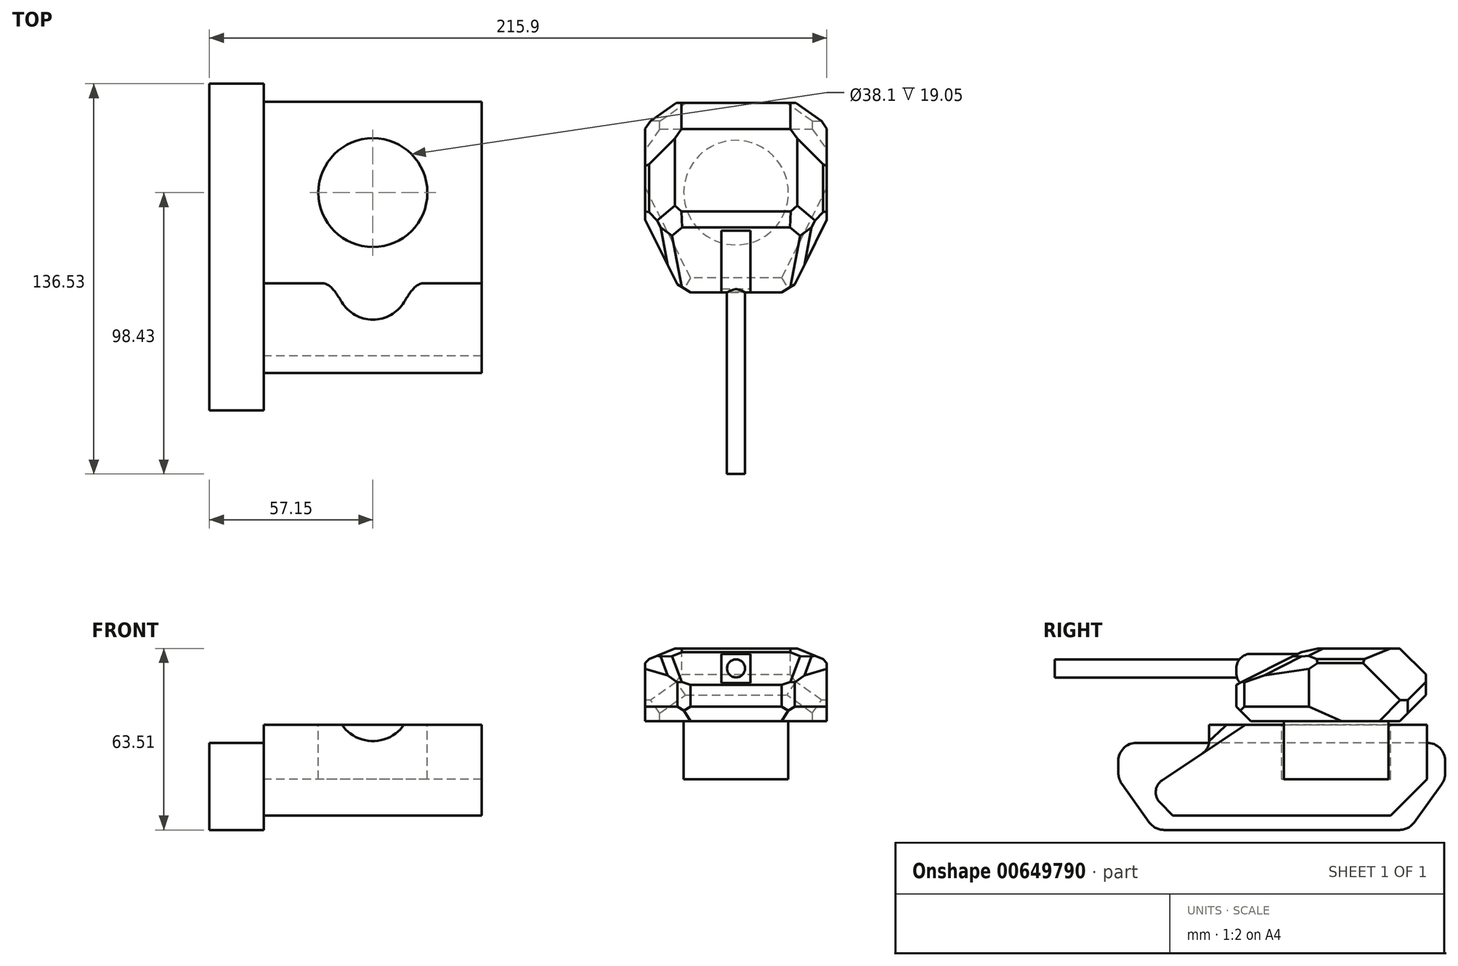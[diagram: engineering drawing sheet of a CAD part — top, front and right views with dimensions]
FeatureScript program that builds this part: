
annotation { "Feature Type Name" : "Feature", "Feature Type Description" : "" }
export const myFeature = defineFeature(function(context is Context, id is Id, definition is map)
    precondition{}
    {
        {
            var Q0;
            Q0=qCreatedBy(makeId("Right.planeOp"),FACE);
            var sketch = newSketch(context, id + "F0", { "sketchPlane" : qUnion([Q0])});
            skLineSegment(sketch, "E0.bottom", {"start": v(-50.8, -15.87) * mm, "end": v(50.8, -15.87) * mm});
            skLineSegment(sketch, "E0.top", {"start": v(-50.8, 15.88) * mm, "end": v(50.8, 15.88) * mm});
            skLineSegment(sketch, "E0.left", {"start": v(-50.8, -15.87) * mm, "end": v(-50.8, 15.88) * mm});
            skLineSegment(sketch, "E0.right", {"start": v(50.8, -15.87) * mm, "end": v(50.8, 15.88) * mm});
            skPoint(sketch, "E0.middle", {"position": v(0, 0) * mm});
            skSolve(sketch);
        }
        {
            var Q0;
            Q0=makeQuery(id+"F0.imprint","IMPRINT",FACE,{"disambiguationData":[TD([[makeQuery(id+"F0.imprint","IMPRINT",EDGE,{"derivedFrom":sQuery(id+"F0.wireOp",EDGE,"E0.bottom")}),1.0]])]});
            extrude(context, id + "F1", {"entities" : qUnion([Q0]), "endBound" : BoundingType.SYMMETRIC, "depth" : 76.2 * mm, "offsetDistance" : 25.4 * mm});
        }
        {
            var Q0;
            Q0=makeQuery(id+"F1.opExtrude","CAP_FACE",FACE,{"disambiguationData":[OSD([sQuery(id+"F0.wireOp",EDGE,"E0.bottom"),sQuery(id+"F0.wireOp",EDGE,"E0.top"),sQuery(id+"F0.wireOp",EDGE,"E0.left"),sQuery(id+"F0.wireOp",EDGE,"E0.right")])],"isStart":true});
            var sketch = newSketch(context, id + "F2", { "sketchPlane" : qUnion([Q0])});
            skLineSegment(sketch, "E1", {"start": v(-57.15, 9.52) * mm, "end": v(-57.15, -3.18) * mm});
            skLineSegment(sketch, "E2", {"start": v(-57.15, 9.52) * mm, "end": v(57.15, 9.52) * mm});
            skLineSegment(sketch, "E3", {"start": v(57.15, 9.52) * mm, "end": v(57.15, -3.18) * mm});
            skLineSegment(sketch, "E4", {"start": v(57.15, -3.18) * mm, "end": v(44.45, -20.95) * mm});
            skLineSegment(sketch, "E5", {"start": v(44.45, -20.95) * mm, "end": v(-44.45, -20.95) * mm});
            skLineSegment(sketch, "E6", {"start": v(-57.15, -3.18) * mm, "end": v(-44.45, -20.96) * mm});
            skSolve(sketch);
        }
        {
            var Q0;
            Q0=makeQuery(id+"F1.opExtrude","SWEPT_EDGE",EDGE,{"disambiguationData":[OSD([sQuery(id+"F0.wireOp",EDGE,"E0.bottom"),sQuery(id+"F0.wireOp",EDGE,"E0.left")])]});
            var Q1;
            Q1=makeQuery(id+"F1.opExtrude","SWEPT_EDGE",EDGE,{"disambiguationData":[OSD([sQuery(id+"F0.wireOp",EDGE,"E0.bottom"),sQuery(id+"F0.wireOp",EDGE,"E0.right")])]});
            chamfer(context, id + "F3", {"entities" : qUnion([Q0, Q1]), "width" : 12.7 * mm, "tangentPropagation" : true});
        }
        {
            var Q0;
            Q0 = qSketchRegion(id + "F2", true);
            extrude(context, id + "F4", {"entities" : qUnion([Q0]), "operationType" : NewBodyOperationType.ADD, "depth" : 19.05 * mm, "offsetDistance" : 25.4 * mm});
        }
        {
            var Q0;
            Q0=makeQuery(id+"F4.opExtrude","SWEPT_EDGE",EDGE,{"disambiguationData":[OSD([sQuery(id+"F2.wireOp",EDGE,"E4"),sQuery(id+"F2.wireOp",EDGE,"E5")])]});
            var Q1;
            Q1=makeQuery(id+"F4.opExtrude","SWEPT_EDGE",EDGE,{"disambiguationData":[OSD([sQuery(id+"F2.wireOp",EDGE,"E3"),sQuery(id+"F2.wireOp",EDGE,"E4")])]});
            var Q2;
            Q2=makeQuery(id+"F4.opExtrude","SWEPT_EDGE",EDGE,{"disambiguationData":[OSD([sQuery(id+"F2.wireOp",EDGE,"E2"),sQuery(id+"F2.wireOp",EDGE,"E3")])]});
            var Q3;
            Q3=makeQuery(id+"F4.opExtrude","SWEPT_EDGE",EDGE,{"disambiguationData":[OSD([sQuery(id+"F2.wireOp",EDGE,"E1"),sQuery(id+"F2.wireOp",EDGE,"E2")])]});
            var Q4;
            Q4=makeQuery(id+"F4.opExtrude","SWEPT_EDGE",EDGE,{"disambiguationData":[OSD([sQuery(id+"F2.wireOp",EDGE,"E1"),sQuery(id+"F2.wireOp",EDGE,"E6")])]});
            var Q5;
            Q5=makeQuery(id+"F4.opExtrude","SWEPT_EDGE",EDGE,{"disambiguationData":[OSD([sQuery(id+"F2.wireOp",EDGE,"E5"),sQuery(id+"F2.wireOp",EDGE,"E6")])]});
            fillet(context, id + "F5", {"entities" : qUnion([Q0, Q1, Q2, Q3, Q4, Q5]), "radius" : 6.35 * mm, "tangentPropagation" : true, "allowEdgeOverflow" : false});
        }
        {
            var Q0;
            Q0=makeQuery(id+"F1.opExtrude","SWEPT_EDGE",EDGE,{"disambiguationData":[OSD([sQuery(id+"F0.wireOp",EDGE,"E0.top"),sQuery(id+"F0.wireOp",EDGE,"E0.left")])]});
            chamfer(context, id + "F6", {"entities" : qUnion([Q0]), "chamferType" : ChamferType.TWO_OFFSETS, "width1" : 25.4 * mm, "oppositeDirection" : false, "width2" : 38.1 * mm, "tangentPropagation" : true});
        }
        {
            var Q0;
            {var subQ0=sQuery(id+"F0.wireOp",EDGE,"E0.left");Q0=makeQuery(id+"F6.opChamfer","BLEND_EDGE",EDGE,{"blendedFrom":[makeQuery(id+"F1.opExtrude","SWEPT_EDGE",EDGE,{"disambiguationData":[OSD([sQuery(id+"F0.wireOp",EDGE,"E0.top"),subQ0])]}),makeQuery(id+"F3.opChamfer","BLEND_FACE",FACE,{"disambiguationData":[OSD([sQuery(id+"F0.wireOp",EDGE,"E0.bottom"),subQ0])]})],"blendedInto":[makeQuery(id+"F3.opChamfer","BLEND_FACE",FACE,{"disambiguationData":[OSD([sQuery(id+"F0.wireOp",EDGE,"E0.bottom"),subQ0])]})]});}
            fillet(context, id + "F7", {"entities" : qUnion([Q0]), "radius" : 5.08 * mm, "tangentPropagation" : true, "allowEdgeOverflow" : false});
        }
        {
            var Q0;
            Q0=makeQuery(id+"F1.opExtrude","SWEPT_FACE",FACE,{"disambiguationData":[OSD([sQuery(id+"F0.wireOp",EDGE,"E0.top")])]});
            var sketch = newSketch(context, id + "F8", { "sketchPlane" : qUnion([Q0])});
            skCircle(sketch, "E7", {"center": v(0, 19.05) * mm, "radius": 19.05 * mm});
            skPoint(sketch, "E7.centerSnap0", {"position": v(0, -12.7) * mm});
            skPoint(sketch, "E7.centerSnap1", {"position": v(-38.1, 19.05) * mm});
            skSolve(sketch);
        }
        {
            var Q0;
            Q0=makeQuery(id+"F8.imprint","IMPRINT",FACE,{"disambiguationData":[TD([[makeQuery(id+"F8.imprint","IMPRINT",EDGE,{"derivedFrom":sQuery(id+"F8.wireOp",EDGE,"E7")}),1.0]])]});
            extrude(context, id + "F9", {"entities" : qUnion([Q0]), "operationType" : NewBodyOperationType.REMOVE, "oppositeDirection" : true, "depth" : 19.05 * mm, "offsetDistance" : 25.4 * mm});
        }
        {
            var Q0;
            Q0=makeQuery(id+"F9.boolean.opBoolean","COPY",FACE,{"derivedFrom":makeQuery(id+"F9.opExtrude","CAP_FACE",FACE,{"disambiguationData":[OSD([sQuery(id+"F8.wireOp",EDGE,"E7")])],"isStart":false})});
            var sketch = newSketch(context, id + "F10", { "sketchPlane" : qUnion([Q0])});
            skPoint(sketch, "E8", {"position": v(0, 19.05) * mm});
            skCircle(sketch, "E9", {"center": v(127, 19.05) * mm, "radius": 18.29 * mm});
            skSolve(sketch);
        }
        {
            var Q0;
            Q0=makeQuery(id+"F10.imprint","IMPRINT",FACE,{"disambiguationData":[TD([[makeQuery(id+"F10.imprint","IMPRINT",EDGE,{"derivedFrom":sQuery(id+"F10.wireOp",EDGE,"E9")}),1.0]])]});
            extrude(context, id + "F11", {"entities" : qUnion([Q0]), "depth" : 20.32 * mm, "offsetDistance" : 25.4 * mm});
        }
        {
            var Q0;
            Q0=makeQuery(id+"F11.opExtrude","CAP_FACE",FACE,{"disambiguationData":[OSD([sQuery(id+"F10.wireOp",EDGE,"E9")])],"isStart":false});
            var sketch = newSketch(context, id + "F12", { "sketchPlane" : qUnion([Q0])});
            skLineSegment(sketch, "E10.bottom", {"start": v(95.25, -15.88) * mm, "end": v(158.75, -15.88) * mm});
            skLineSegment(sketch, "E10.top", {"start": v(95.25, 53.97) * mm, "end": v(158.75, 53.97) * mm});
            skLineSegment(sketch, "E10.left", {"start": v(95.25, -15.88) * mm, "end": v(95.25, 53.97) * mm});
            skLineSegment(sketch, "E10.right", {"start": v(158.75, -15.88) * mm, "end": v(158.75, 53.97) * mm});
            skPoint(sketch, "E10.middle", {"position": v(127, 19.05) * mm});
            skSolve(sketch);
        }
        {
            var Q0;
            Q0 = qSketchRegion(id + "F12", true);
            extrude(context, id + "F13", {"entities" : qUnion([Q0]), "operationType" : NewBodyOperationType.ADD, "depth" : 25.4 * mm, "offsetDistance" : 25.4 * mm});
        }
        {
            var Q0;
            Q0=makeQuery(id+"F13.opExtrude","SWEPT_EDGE",EDGE,{"disambiguationData":[OSD([sQuery(id+"F12.wireOp",EDGE,"E10.bottom"),sQuery(id+"F12.wireOp",EDGE,"E10.left")])]});
            var Q1;
            Q1=makeQuery(id+"F13.opExtrude","SWEPT_EDGE",EDGE,{"disambiguationData":[OSD([sQuery(id+"F12.wireOp",EDGE,"E10.bottom"),sQuery(id+"F12.wireOp",EDGE,"E10.right")])]});
            chamfer(context, id + "F14", {"entities" : qUnion([Q0, Q1]), "chamferType" : ChamferType.TWO_OFFSETS, "width1" : 12.7 * mm, "oppositeDirection" : false, "width2" : 25.4 * mm, "tangentPropagation" : true});
        }
        {
            var Q0;
            Q0=makeQuery(id+"F13.opExtrude","CAP_EDGE",EDGE,{"disambiguationData":[OSD([sQuery(id+"F12.wireOp",EDGE,"E10.bottom")])],"isStart":false});
            chamfer(context, id + "F15", {"entities" : qUnion([Q0]), "chamferType" : ChamferType.TWO_OFFSETS, "width1" : 25.4 * mm, "oppositeDirection" : false, "width2" : 12.7 * mm, "tangentPropagation" : true});
        }
        {
            var Q0;
            Q0=makeQuery(id+"F13.opExtrude","CAP_EDGE",EDGE,{"disambiguationData":[OSD([sQuery(id+"F12.wireOp",EDGE,"E10.right")])],"isStart":false});
            var Q1;
            Q1=makeQuery(id+"F13.opExtrude","CAP_EDGE",EDGE,{"disambiguationData":[OSD([sQuery(id+"F12.wireOp",EDGE,"E10.left")])],"isStart":false});
            chamfer(context, id + "F16", {"entities" : qUnion([Q0, Q1]), "width" : 5.08 * mm, "tangentPropagation" : true});
        }
        {
            var Q0;
            Q0=makeQuery(id+"F13.opExtrude","CAP_EDGE",EDGE,{"disambiguationData":[OSD([sQuery(id+"F12.wireOp",EDGE,"E10.top")])],"isStart":true});
            chamfer(context, id + "F17", {"entities" : qUnion([Q0]), "width" : 12.7 * mm, "tangentPropagation" : true});
        }
        {
            var Q0;
            Q0=makeQuery(id+"F17.opChamfer","BLEND_EDGE",EDGE,{"blendedFrom":[makeQuery(id+"F13.opExtrude","CAP_EDGE",EDGE,{"disambiguationData":[OSD([sQuery(id+"F12.wireOp",EDGE,"E10.top")])],"isStart":true}),makeQuery(id+"F13.opExtrude","SWEPT_FACE",FACE,{"disambiguationData":[OSD([sQuery(id+"F12.wireOp",EDGE,"E10.right")])]})],"blendedInto":[makeQuery(id+"F13.opExtrude","SWEPT_FACE",FACE,{"disambiguationData":[OSD([sQuery(id+"F12.wireOp",EDGE,"E10.right")])]})]});
            var Q1;
            Q1=makeQuery(id+"F17.opChamfer","BLEND_EDGE",EDGE,{"blendedFrom":[makeQuery(id+"F13.opExtrude","CAP_EDGE",EDGE,{"disambiguationData":[OSD([sQuery(id+"F12.wireOp",EDGE,"E10.top")])],"isStart":true}),makeQuery(id+"F13.opExtrude","SWEPT_FACE",FACE,{"disambiguationData":[OSD([sQuery(id+"F12.wireOp",EDGE,"E10.left")])]})],"blendedInto":[makeQuery(id+"F13.opExtrude","SWEPT_FACE",FACE,{"disambiguationData":[OSD([sQuery(id+"F12.wireOp",EDGE,"E10.left")])]})]});
            chamfer(context, id + "F18", {"entities" : qUnion([Q0, Q1]), "width" : 5.08 * mm, "tangentPropagation" : true});
        }
        {
            var Q0;
            Q0=makeQuery(id+"F13.opExtrude","CAP_EDGE",EDGE,{"disambiguationData":[OSD([sQuery(id+"F12.wireOp",EDGE,"E10.bottom")])],"isStart":true});
            var Q1;
            {var subQ0=sQuery(id+"F12.wireOp",EDGE,"E10.right");var subQ1=sQuery(id+"F12.wireOp",EDGE,"E10.bottom");Q1=makeQuery(id+"F14.opChamfer","BLEND_EDGE",EDGE,{"blendedFrom":[makeQuery(id+"F13.opExtrude","SWEPT_EDGE",EDGE,{"disambiguationData":[OSD([subQ1,subQ0])]}),makeQuery(id+"F13.opExtrude","CAP_FACE",FACE,{"disambiguationData":[OSD([subQ1,sQuery(id+"F12.wireOp",EDGE,"E10.top"),sQuery(id+"F12.wireOp",EDGE,"E10.left"),subQ0])],"isStart":true})],"blendedInto":[makeQuery(id+"F13.opExtrude","CAP_FACE",FACE,{"disambiguationData":[OSD([subQ1,sQuery(id+"F12.wireOp",EDGE,"E10.top"),sQuery(id+"F12.wireOp",EDGE,"E10.left"),subQ0])],"isStart":true})]});}
            var Q2;
            {var subQ0=sQuery(id+"F12.wireOp",EDGE,"E10.left");var subQ1=sQuery(id+"F12.wireOp",EDGE,"E10.bottom");Q2=makeQuery(id+"F14.opChamfer","BLEND_EDGE",EDGE,{"blendedFrom":[makeQuery(id+"F13.opExtrude","SWEPT_EDGE",EDGE,{"disambiguationData":[OSD([subQ1,subQ0])]}),makeQuery(id+"F13.opExtrude","CAP_FACE",FACE,{"disambiguationData":[OSD([subQ1,sQuery(id+"F12.wireOp",EDGE,"E10.top"),subQ0,sQuery(id+"F12.wireOp",EDGE,"E10.right")])],"isStart":true})],"blendedInto":[makeQuery(id+"F13.opExtrude","CAP_FACE",FACE,{"disambiguationData":[OSD([subQ1,sQuery(id+"F12.wireOp",EDGE,"E10.top"),subQ0,sQuery(id+"F12.wireOp",EDGE,"E10.right")])],"isStart":true})]});}
            chamfer(context, id + "F19", {"entities" : qUnion([Q0, Q1, Q2]), "width" : 5.08 * mm, "tangentPropagation" : true});
        }
        {
            var Q0;
            Q0=makeQuery(id+"F13.opExtrude","SWEPT_FACE",FACE,{"disambiguationData":[OSD([sQuery(id+"F12.wireOp",EDGE,"E10.bottom")])]});
            var sketch = newSketch(context, id + "F20", { "sketchPlane" : qUnion([Q0])});
            skPoint(sketch, "E11", {"position": v(127, 29.85) * mm});
            skLineSegment(sketch, "E12.bottom", {"start": v(121.92, 30.48) * mm, "end": v(132.08, 30.48) * mm});
            skLineSegment(sketch, "E12.top", {"start": v(121.92, 40.64) * mm, "end": v(132.08, 40.64) * mm});
            skLineSegment(sketch, "E12.left", {"start": v(121.92, 30.48) * mm, "end": v(121.92, 40.64) * mm});
            skLineSegment(sketch, "E12.right", {"start": v(132.08, 30.48) * mm, "end": v(132.08, 40.64) * mm});
            skPoint(sketch, "E12.middle", {"position": v(127, 35.56) * mm});
            skSolve(sketch);
        }
        {
            var Q0;
            Q0=makeQuery(id+"F20.imprint","IMPRINT",FACE,{"disambiguationData":[TD([[makeQuery(id+"F20.imprint","IMPRINT",EDGE,{"derivedFrom":sQuery(id+"F20.wireOp",EDGE,"E12.bottom")}),1.0]])]});
            extrude(context, id + "F21", {"entities" : qUnion([Q0]), "operationType" : NewBodyOperationType.ADD, "oppositeDirection" : true, "depth" : 25.4 * mm, "offsetDistance" : 25.4 * mm});
        }
        {
            var Q0;
            Q0=makeQuery(id+"F21.opExtrude","CAP_EDGE",EDGE,{"disambiguationData":[OSD([sQuery(id+"F20.wireOp",EDGE,"E12.bottom")])],"isStart":true});
            var Q1;
            Q1=makeQuery(id+"F21.opExtrude","CAP_EDGE",EDGE,{"disambiguationData":[OSD([sQuery(id+"F20.wireOp",EDGE,"E12.top")])],"isStart":true});
            fillet(context, id + "F22", {"entities" : qUnion([Q0, Q1]), "radius" : 5.08 * mm, "tangentPropagation" : true, "allowEdgeOverflow" : false});
        }
        {
            var Q0;
            Q0=makeQuery(id+"F21.opExtrude","CAP_FACE",FACE,{"disambiguationData":[OSD([sQuery(id+"F20.wireOp",EDGE,"E12.bottom"),sQuery(id+"F20.wireOp",EDGE,"E12.top"),sQuery(id+"F20.wireOp",EDGE,"E12.left"),sQuery(id+"F20.wireOp",EDGE,"E12.right")])],"isStart":true});
            var sketch = newSketch(context, id + "F23", { "sketchPlane" : qUnion([Q0])});
            skPoint(sketch, "E13", {"position": v(127, 40.64) * mm});
            skPoint(sketch, "E14", {"position": v(121.92, 35.56) * mm});
            skCircle(sketch, "E15", {"center": v(127, 35.56) * mm, "radius": 3.18 * mm});
            skSolve(sketch);
        }
        {
            var Q0;
            Q0 = qSketchRegion(id + "F23", true);
            extrude(context, id + "F24", {"entities" : qUnion([Q0]), "operationType" : NewBodyOperationType.ADD, "endBound" : BoundingType.SYMMETRIC, "depth" : 25.4 * mm, "offsetDistance" : 25.4 * mm});
        }
        {
            var Q0;
            Q0=makeQuery(id+"F24.opExtrude","CAP_FACE",FACE,{"disambiguationData":[OSD([sQuery(id+"F23.wireOp",EDGE,"E15")])],"isStart":false});
            extrude(context, id + "F25", {"entities" : qUnion([Q0]), "operationType" : NewBodyOperationType.ADD, "depth" : 50.8 * mm, "offsetDistance" : 25.4 * mm});
        }
        {
            var Q0;
            Q0=makeQuery(id+"F13.opExtrude","CAP_FACE",FACE,{"disambiguationData":[OSD([sQuery(id+"F12.wireOp",EDGE,"E10.bottom"),sQuery(id+"F12.wireOp",EDGE,"E10.top"),sQuery(id+"F12.wireOp",EDGE,"E10.left"),sQuery(id+"F12.wireOp",EDGE,"E10.right")])],"isStart":false});
            chamfer(context, id + "F26", {"entities" : qUnion([Q0]), "width" : 12.7 * mm, "tangentPropagation" : true});
        }
        {
            var Q0;
            {var subQ0=sQuery(id+"F12.wireOp",EDGE,"E10.bottom");var subQ1=sQuery(id+"F12.wireOp",EDGE,"E10.left");Q0=makeQuery(id+"F26.opChamfer","BLEND_EDGE",EDGE,{"blendedFrom":[makeQuery(id+"F16.opChamfer","BLEND_EDGE",EDGE,{"blendedFrom":[makeQuery(id+"F13.opExtrude","CAP_EDGE",EDGE,{"disambiguationData":[OSD([subQ1])],"isStart":false}),makeQuery(id+"F13.opExtrude","CAP_FACE",FACE,{"disambiguationData":[OSD([subQ0,sQuery(id+"F12.wireOp",EDGE,"E10.top"),subQ1,sQuery(id+"F12.wireOp",EDGE,"E10.right")])],"isStart":false})],"blendedInto":[makeQuery(id+"F13.opExtrude","CAP_FACE",FACE,{"disambiguationData":[OSD([subQ0,sQuery(id+"F12.wireOp",EDGE,"E10.top"),subQ1,sQuery(id+"F12.wireOp",EDGE,"E10.right")])],"isStart":false})]}),makeQuery(id+"F15.opChamfer","BLEND_FACE",FACE,{"disambiguationData":[OSD([subQ0])]})],"blendedInto":[makeQuery(id+"F15.opChamfer","BLEND_FACE",FACE,{"disambiguationData":[OSD([subQ0])]})]});}
            var Q1;
            {var subQ0=sQuery(id+"F12.wireOp",EDGE,"E10.bottom");var subQ1=sQuery(id+"F12.wireOp",EDGE,"E10.right");Q1=makeQuery(id+"F26.opChamfer","BLEND_EDGE",EDGE,{"blendedFrom":[makeQuery(id+"F16.opChamfer","BLEND_EDGE",EDGE,{"blendedFrom":[makeQuery(id+"F13.opExtrude","CAP_EDGE",EDGE,{"disambiguationData":[OSD([subQ1])],"isStart":false}),makeQuery(id+"F13.opExtrude","CAP_FACE",FACE,{"disambiguationData":[OSD([subQ0,sQuery(id+"F12.wireOp",EDGE,"E10.top"),sQuery(id+"F12.wireOp",EDGE,"E10.left"),subQ1])],"isStart":false})],"blendedInto":[makeQuery(id+"F13.opExtrude","CAP_FACE",FACE,{"disambiguationData":[OSD([subQ0,sQuery(id+"F12.wireOp",EDGE,"E10.top"),sQuery(id+"F12.wireOp",EDGE,"E10.left"),subQ1])],"isStart":false})]}),makeQuery(id+"F15.opChamfer","BLEND_FACE",FACE,{"disambiguationData":[OSD([subQ0])]})],"blendedInto":[makeQuery(id+"F15.opChamfer","BLEND_FACE",FACE,{"disambiguationData":[OSD([subQ0])]})]});}
            chamfer(context, id + "F27", {"entities" : qUnion([Q0, Q1]), "width" : 12.7 * mm, "tangentPropagation" : true});
        }
        {
            var Q0;
            {var subQ0=sQuery(id+"F12.wireOp",EDGE,"E10.left");var subQ1=sQuery(id+"F12.wireOp",EDGE,"E10.bottom");Q0=makeQuery(id+"F27.opChamfer","BLEND_EDGE",EDGE,{"blendedFrom":[makeQuery(id+"F26.opChamfer","BLEND_EDGE",EDGE,{"blendedFrom":[makeQuery(id+"F16.opChamfer","BLEND_EDGE",EDGE,{"blendedFrom":[makeQuery(id+"F13.opExtrude","CAP_EDGE",EDGE,{"disambiguationData":[OSD([subQ0])],"isStart":false}),makeQuery(id+"F13.opExtrude","CAP_FACE",FACE,{"disambiguationData":[OSD([subQ1,sQuery(id+"F12.wireOp",EDGE,"E10.top"),subQ0,sQuery(id+"F12.wireOp",EDGE,"E10.right")])],"isStart":false})],"blendedInto":[makeQuery(id+"F13.opExtrude","CAP_FACE",FACE,{"disambiguationData":[OSD([subQ1,sQuery(id+"F12.wireOp",EDGE,"E10.top"),subQ0,sQuery(id+"F12.wireOp",EDGE,"E10.right")])],"isStart":false})]}),makeQuery(id+"F15.opChamfer","BLEND_FACE",FACE,{"disambiguationData":[OSD([subQ1])]})],"blendedInto":[makeQuery(id+"F15.opChamfer","BLEND_FACE",FACE,{"disambiguationData":[OSD([subQ1])]})]}),makeQuery(id+"F14.opChamfer","BLEND_FACE",FACE,{"disambiguationData":[OSD([subQ1,subQ0])]})],"blendedInto":[makeQuery(id+"F14.opChamfer","BLEND_FACE",FACE,{"disambiguationData":[OSD([subQ1,subQ0])]})]});}
            var Q1;
            {var subQ0=sQuery(id+"F12.wireOp",EDGE,"E10.right");var subQ1=sQuery(id+"F12.wireOp",EDGE,"E10.bottom");Q1=makeQuery(id+"F27.opChamfer","BLEND_EDGE",EDGE,{"blendedFrom":[makeQuery(id+"F26.opChamfer","BLEND_EDGE",EDGE,{"blendedFrom":[makeQuery(id+"F16.opChamfer","BLEND_EDGE",EDGE,{"blendedFrom":[makeQuery(id+"F13.opExtrude","CAP_EDGE",EDGE,{"disambiguationData":[OSD([subQ0])],"isStart":false}),makeQuery(id+"F13.opExtrude","CAP_FACE",FACE,{"disambiguationData":[OSD([subQ1,sQuery(id+"F12.wireOp",EDGE,"E10.top"),sQuery(id+"F12.wireOp",EDGE,"E10.left"),subQ0])],"isStart":false})],"blendedInto":[makeQuery(id+"F13.opExtrude","CAP_FACE",FACE,{"disambiguationData":[OSD([subQ1,sQuery(id+"F12.wireOp",EDGE,"E10.top"),sQuery(id+"F12.wireOp",EDGE,"E10.left"),subQ0])],"isStart":false})]}),makeQuery(id+"F15.opChamfer","BLEND_FACE",FACE,{"disambiguationData":[OSD([subQ1])]})],"blendedInto":[makeQuery(id+"F15.opChamfer","BLEND_FACE",FACE,{"disambiguationData":[OSD([subQ1])]})]}),makeQuery(id+"F14.opChamfer","BLEND_FACE",FACE,{"disambiguationData":[OSD([subQ1,subQ0])]})],"blendedInto":[makeQuery(id+"F14.opChamfer","BLEND_FACE",FACE,{"disambiguationData":[OSD([subQ1,subQ0])]})]});}
            chamfer(context, id + "F28", {"entities" : qUnion([Q0, Q1]), "width" : 5.08 * mm, "tangentPropagation" : true});
        }
        {
            var Q0;
            {var subQ0=sQuery(id+"F12.wireOp",EDGE,"E10.top");Q0=makeQuery(id+"F26.opChamfer","BLEND_EDGE",EDGE,{"blendedFrom":[makeQuery(id+"F13.opExtrude","CAP_EDGE",EDGE,{"disambiguationData":[OSD([subQ0])],"isStart":false}),makeQuery(id+"F17.opChamfer","BLEND_FACE",FACE,{"disambiguationData":[OSD([subQ0])]})],"blendedInto":[makeQuery(id+"F17.opChamfer","BLEND_FACE",FACE,{"disambiguationData":[OSD([subQ0])]})]});}
            chamfer(context, id + "F29", {"entities" : qUnion([Q0]), "width" : 5.08 * mm, "tangentPropagation" : true});
        }
        {
            var Q0;
            {var subQ0=sQuery(id+"F12.wireOp",EDGE,"E10.bottom");Q0=makeQuery(id+"F14.opChamfer","BLEND_EDGE",EDGE,{"blendedFrom":[makeQuery(id+"F13.opExtrude","SWEPT_EDGE",EDGE,{"disambiguationData":[OSD([subQ0,sQuery(id+"F12.wireOp",EDGE,"E10.right")])]}),makeQuery(id+"F13.opExtrude","SWEPT_FACE",FACE,{"disambiguationData":[OSD([subQ0])]})],"blendedInto":[makeQuery(id+"F13.opExtrude","SWEPT_FACE",FACE,{"disambiguationData":[OSD([subQ0])]})]});}
            var Q1;
            {var subQ0=sQuery(id+"F12.wireOp",EDGE,"E10.bottom");Q1=makeQuery(id+"F14.opChamfer","BLEND_EDGE",EDGE,{"blendedFrom":[makeQuery(id+"F13.opExtrude","SWEPT_EDGE",EDGE,{"disambiguationData":[OSD([subQ0,sQuery(id+"F12.wireOp",EDGE,"E10.left")])]}),makeQuery(id+"F13.opExtrude","SWEPT_FACE",FACE,{"disambiguationData":[OSD([subQ0])]})],"blendedInto":[makeQuery(id+"F13.opExtrude","SWEPT_FACE",FACE,{"disambiguationData":[OSD([subQ0])]})]});}
            var Q2;
            {var subQ0=sQuery(id+"F12.wireOp",EDGE,"E10.bottom");var subQ1=makeQuery(id+"F15.opChamfer","BLEND_FACE",FACE,{"disambiguationData":[OSD([subQ0])]});var subQ2=sQuery(id+"F12.wireOp",EDGE,"E10.left");Q2=makeQuery(id+"F28.opChamfer","BLEND_EDGE",EDGE,{"blendedFrom":[makeQuery(id+"F27.opChamfer","BLEND_EDGE",EDGE,{"blendedFrom":[makeQuery(id+"F26.opChamfer","BLEND_EDGE",EDGE,{"blendedFrom":[makeQuery(id+"F16.opChamfer","BLEND_EDGE",EDGE,{"blendedFrom":[makeQuery(id+"F13.opExtrude","CAP_EDGE",EDGE,{"disambiguationData":[OSD([subQ2])],"isStart":false}),makeQuery(id+"F13.opExtrude","CAP_FACE",FACE,{"disambiguationData":[OSD([subQ0,sQuery(id+"F12.wireOp",EDGE,"E10.top"),subQ2,sQuery(id+"F12.wireOp",EDGE,"E10.right")])],"isStart":false})],"blendedInto":[makeQuery(id+"F13.opExtrude","CAP_FACE",FACE,{"disambiguationData":[OSD([subQ0,sQuery(id+"F12.wireOp",EDGE,"E10.top"),subQ2,sQuery(id+"F12.wireOp",EDGE,"E10.right")])],"isStart":false})]}),subQ1],"blendedInto":[subQ1]}),makeQuery(id+"F14.opChamfer","BLEND_FACE",FACE,{"disambiguationData":[OSD([subQ0,subQ2])]})],"blendedInto":[makeQuery(id+"F14.opChamfer","BLEND_FACE",FACE,{"disambiguationData":[OSD([subQ0,subQ2])]})]}),subQ1],"blendedInto":[subQ1]});}
            var Q3;
            {var subQ0=sQuery(id+"F12.wireOp",EDGE,"E10.bottom");var subQ1=makeQuery(id+"F15.opChamfer","BLEND_FACE",FACE,{"disambiguationData":[OSD([subQ0])]});var subQ2=sQuery(id+"F12.wireOp",EDGE,"E10.right");Q3=makeQuery(id+"F28.opChamfer","BLEND_EDGE",EDGE,{"blendedFrom":[makeQuery(id+"F27.opChamfer","BLEND_EDGE",EDGE,{"blendedFrom":[makeQuery(id+"F26.opChamfer","BLEND_EDGE",EDGE,{"blendedFrom":[makeQuery(id+"F16.opChamfer","BLEND_EDGE",EDGE,{"blendedFrom":[makeQuery(id+"F13.opExtrude","CAP_EDGE",EDGE,{"disambiguationData":[OSD([subQ2])],"isStart":false}),makeQuery(id+"F13.opExtrude","CAP_FACE",FACE,{"disambiguationData":[OSD([subQ0,sQuery(id+"F12.wireOp",EDGE,"E10.top"),sQuery(id+"F12.wireOp",EDGE,"E10.left"),subQ2])],"isStart":false})],"blendedInto":[makeQuery(id+"F13.opExtrude","CAP_FACE",FACE,{"disambiguationData":[OSD([subQ0,sQuery(id+"F12.wireOp",EDGE,"E10.top"),sQuery(id+"F12.wireOp",EDGE,"E10.left"),subQ2])],"isStart":false})]}),subQ1],"blendedInto":[subQ1]}),makeQuery(id+"F14.opChamfer","BLEND_FACE",FACE,{"disambiguationData":[OSD([subQ0,subQ2])]})],"blendedInto":[makeQuery(id+"F14.opChamfer","BLEND_FACE",FACE,{"disambiguationData":[OSD([subQ0,subQ2])]})]}),subQ1],"blendedInto":[subQ1]});}
            chamfer(context, id + "F30", {"entities" : qUnion([Q0, Q1, Q2, Q3]), "width" : 5.08 * mm, "tangentPropagation" : true});
        }
        {
            var Q0;
            Q0=makeQuery(id+"F26.opChamfer","BLEND_EDGE",EDGE,{"blendedFrom":[makeQuery(id+"F13.opExtrude","CAP_EDGE",EDGE,{"disambiguationData":[OSD([sQuery(id+"F12.wireOp",EDGE,"E10.top")])],"isStart":false}),makeQuery(id+"F13.opExtrude","SWEPT_FACE",FACE,{"disambiguationData":[OSD([sQuery(id+"F12.wireOp",EDGE,"E10.left")])]})],"blendedInto":[makeQuery(id+"F13.opExtrude","SWEPT_FACE",FACE,{"disambiguationData":[OSD([sQuery(id+"F12.wireOp",EDGE,"E10.left")])]})]});
            var Q1;
            {var subQ0=sQuery(id+"F12.wireOp",EDGE,"E10.top");Q1=makeQuery(id+"F29.opChamfer","BLEND_EDGE",EDGE,{"blendedFrom":[makeQuery(id+"F26.opChamfer","BLEND_EDGE",EDGE,{"blendedFrom":[makeQuery(id+"F13.opExtrude","CAP_EDGE",EDGE,{"disambiguationData":[OSD([subQ0])],"isStart":false}),makeQuery(id+"F17.opChamfer","BLEND_FACE",FACE,{"disambiguationData":[OSD([subQ0])]})],"blendedInto":[makeQuery(id+"F17.opChamfer","BLEND_FACE",FACE,{"disambiguationData":[OSD([subQ0])]})]}),makeQuery(id+"F18.opChamfer","BLEND_FACE",FACE,{"disambiguationData":[OSD([subQ0,sQuery(id+"F12.wireOp",EDGE,"E10.left")])]})],"blendedInto":[makeQuery(id+"F18.opChamfer","BLEND_FACE",FACE,{"disambiguationData":[OSD([subQ0,sQuery(id+"F12.wireOp",EDGE,"E10.left")])]})]});}
            var Q2;
            Q2=makeQuery(id+"F26.opChamfer","BLEND_EDGE",EDGE,{"blendedFrom":[makeQuery(id+"F13.opExtrude","CAP_EDGE",EDGE,{"disambiguationData":[OSD([sQuery(id+"F12.wireOp",EDGE,"E10.top")])],"isStart":false}),makeQuery(id+"F13.opExtrude","SWEPT_FACE",FACE,{"disambiguationData":[OSD([sQuery(id+"F12.wireOp",EDGE,"E10.right")])]})],"blendedInto":[makeQuery(id+"F13.opExtrude","SWEPT_FACE",FACE,{"disambiguationData":[OSD([sQuery(id+"F12.wireOp",EDGE,"E10.right")])]})]});
            var Q3;
            {var subQ0=sQuery(id+"F12.wireOp",EDGE,"E10.top");Q3=makeQuery(id+"F29.opChamfer","BLEND_EDGE",EDGE,{"blendedFrom":[makeQuery(id+"F26.opChamfer","BLEND_EDGE",EDGE,{"blendedFrom":[makeQuery(id+"F13.opExtrude","CAP_EDGE",EDGE,{"disambiguationData":[OSD([subQ0])],"isStart":false}),makeQuery(id+"F17.opChamfer","BLEND_FACE",FACE,{"disambiguationData":[OSD([subQ0])]})],"blendedInto":[makeQuery(id+"F17.opChamfer","BLEND_FACE",FACE,{"disambiguationData":[OSD([subQ0])]})]}),makeQuery(id+"F18.opChamfer","BLEND_FACE",FACE,{"disambiguationData":[OSD([subQ0,sQuery(id+"F12.wireOp",EDGE,"E10.right")])]})],"blendedInto":[makeQuery(id+"F18.opChamfer","BLEND_FACE",FACE,{"disambiguationData":[OSD([subQ0,sQuery(id+"F12.wireOp",EDGE,"E10.right")])]})]});}
            chamfer(context, id + "F31", {"entities" : qUnion([Q0, Q1, Q2, Q3]), "width" : 12.7 * mm, "tangentPropagation" : true});
        }
        {
            var Q0;
            Q0=makeQuery(id+"F1.opExtrude","SWEPT_FACE",FACE,{"disambiguationData":[OSD([sQuery(id+"F0.wireOp",EDGE,"E0.top")])]});
            var sketch = newSketch(context, id + "F32", { "sketchPlane" : qUnion([Q0])});
            skCircle(sketch, "E16", {"center": v(0, -12.7) * mm, "radius": 12.7 * mm});
            skSolve(sketch);
        }
        {
            var Q0;
            {var subQ0=sQuery(id+"F32.wireOp",EDGE,"E16");var subQ1=sQuery(id+"F0.wireOp",EDGE,"E0.top");var subQ2=makeQuery(id+"F6.opChamfer","BLEND_EDGE",EDGE,{"blendedFrom":[makeQuery(id+"F1.opExtrude","SWEPT_EDGE",EDGE,{"disambiguationData":[OSD([subQ1,sQuery(id+"F0.wireOp",EDGE,"E0.left")])]}),makeQuery(id+"F1.opExtrude","SWEPT_FACE",FACE,{"disambiguationData":[OSD([subQ1])]})],"blendedInto":[makeQuery(id+"F1.opExtrude","SWEPT_FACE",FACE,{"disambiguationData":[OSD([subQ1])]})]});var subQ3=makeQuery(id+"F32.imprint","INTERSECT",VERTEX,{"disambiguationData":[OD(0.0)],"derivedFrom":[subQ2,subQ0]});Q0=makeQuery(id+"F32.imprint","IMPRINT",FACE,{"disambiguationData":[TD([[makeQuery(id+"F32.imprint","IMPRINT",EDGE,{"disambiguationData":[TD([[subQ3,1.0]])],"derivedFrom":subQ0}),1.0]])]});}
            extrude(context, id + "F33", {"entities" : qUnion([Q0]), "operationType" : NewBodyOperationType.ADD, "oppositeDirection" : true, "depth" : 25.4 * mm, "offsetDistance" : 25.4 * mm});
        }
        {
            var Q0;
            Q0=makeQuery(id+"F33.boolean.opBoolean","INTERSECT",EDGE,{"derivedFrom":[makeQuery(id+"F6.opChamfer","BLEND_FACE",FACE,{"disambiguationData":[OSD([sQuery(id+"F0.wireOp",EDGE,"E0.top"),sQuery(id+"F0.wireOp",EDGE,"E0.left")])]}),makeQuery(id+"F33.opExtrude","SWEPT_FACE",FACE,{"disambiguationData":[OSD([sQuery(id+"F32.wireOp",EDGE,"E16")])]})]});
            fillet(context, id + "F34", {"entities" : qUnion([Q0]), "radius" : 5.08 * mm, "tangentPropagation" : true, "allowEdgeOverflow" : false});
        }
    });
